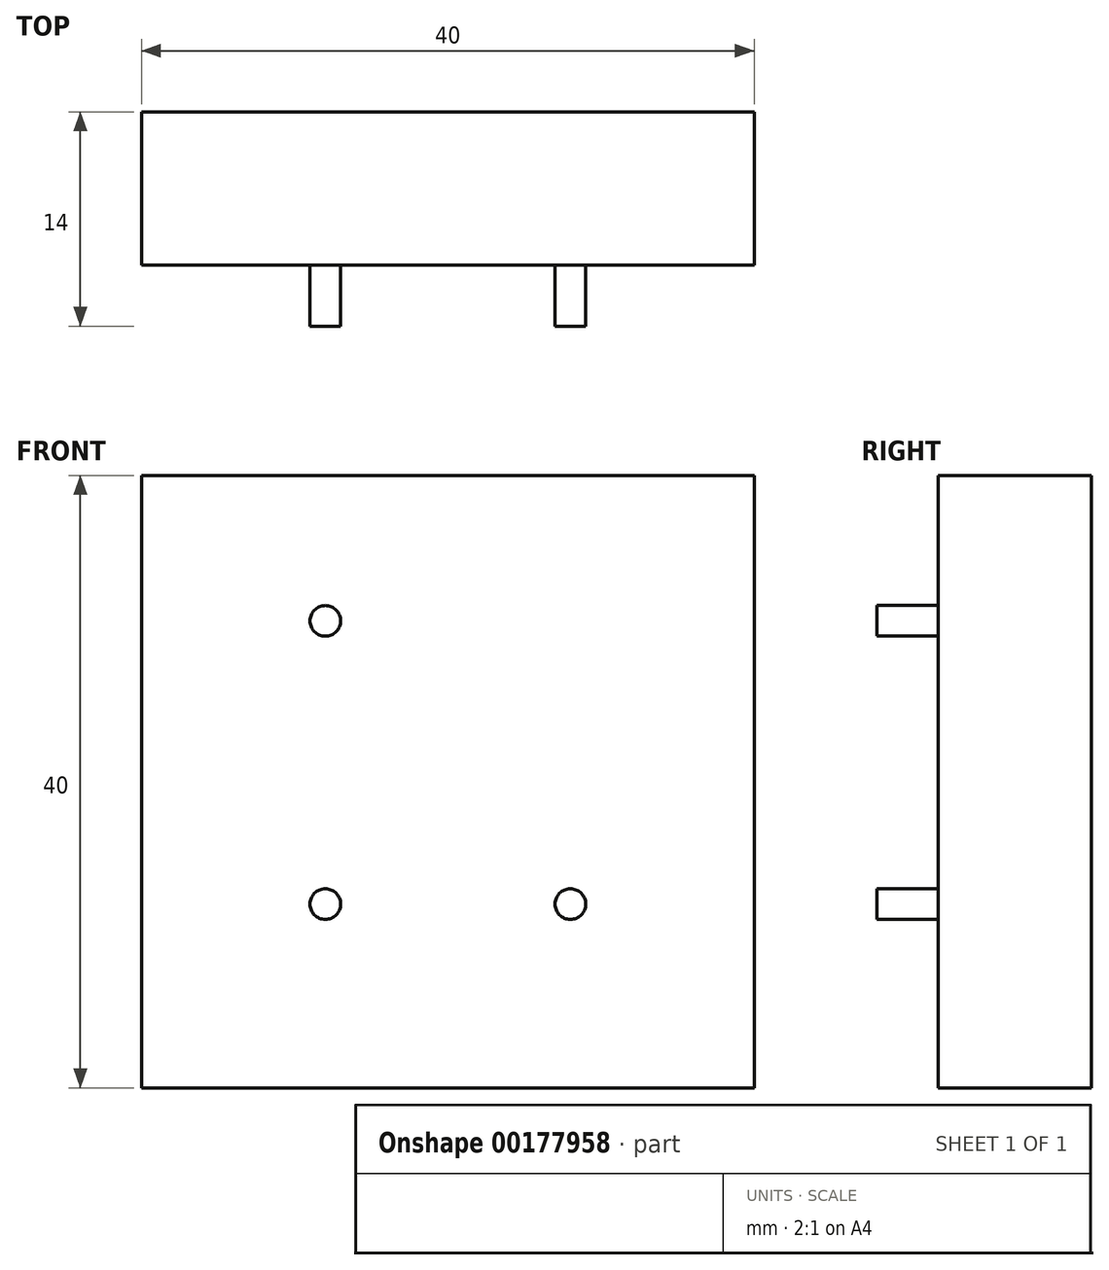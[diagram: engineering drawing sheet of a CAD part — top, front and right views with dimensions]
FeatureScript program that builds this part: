
annotation { "Feature Type Name" : "Feature", "Feature Type Description" : "" }
export const myFeature = defineFeature(function(context is Context, id is Id, definition is map)
    precondition{}
    {
        {
            var Q0;
            Q0=qCreatedBy(makeId("Right.planeOp"),FACE);
            var sketch = newSketch(context, id + "F0", { "sketchPlane" : qUnion([Q0])});
            skLineSegment(sketch, "E0.bottom", {"start": v(-5, -20) * mm, "end": v(5, -20) * mm});
            skLineSegment(sketch, "E0.top", {"start": v(-5, 20) * mm, "end": v(5, 20) * mm});
            skLineSegment(sketch, "E0.left", {"start": v(-5, -20) * mm, "end": v(-5, 20) * mm});
            skLineSegment(sketch, "E0.right", {"start": v(5, -20) * mm, "end": v(5, 20) * mm});
            skPoint(sketch, "E0.middle", {"position": v(0, 0) * mm});
            skSolve(sketch);
        }
        {
            var Q0;
            Q0 = qSketchRegion(id + "F0", true);
            extrude(context, id + "F1", {"entities" : qUnion([Q0]), "depth" : 20 * mm, "hasSecondDirection" : true, "secondDirectionOppositeDirection" : true, "secondDirectionDepth" : 20 * mm});
        }
        {
            var Q0;
            Q0=makeQuery(id+"F1.opExtrude","SWEPT_FACE",FACE,{"disambiguationData":[OSD([sQuery(id+"F0.wireOp",EDGE,"E0.left")])]});
            var sketch = newSketch(context, id + "F2", { "sketchPlane" : qUnion([Q0])});
            skCircle(sketch, "E1", {"center": v(-8, 10.5) * mm, "radius": 1 * mm});
            skCircle(sketch, "E2", {"center": v(-8, -8) * mm, "radius": 1 * mm});
            skCircle(sketch, "E3", {"center": v(8, -8) * mm, "radius": 1 * mm});
            skSolve(sketch);
        }
        {
            var Q0;
            Q0 = qSketchRegion(id + "F2", true);
            extrude(context, id + "F3", {"entities" : qUnion([Q0]), "operationType" : NewBodyOperationType.ADD, "depth" : 4 * mm});
        }
    });
